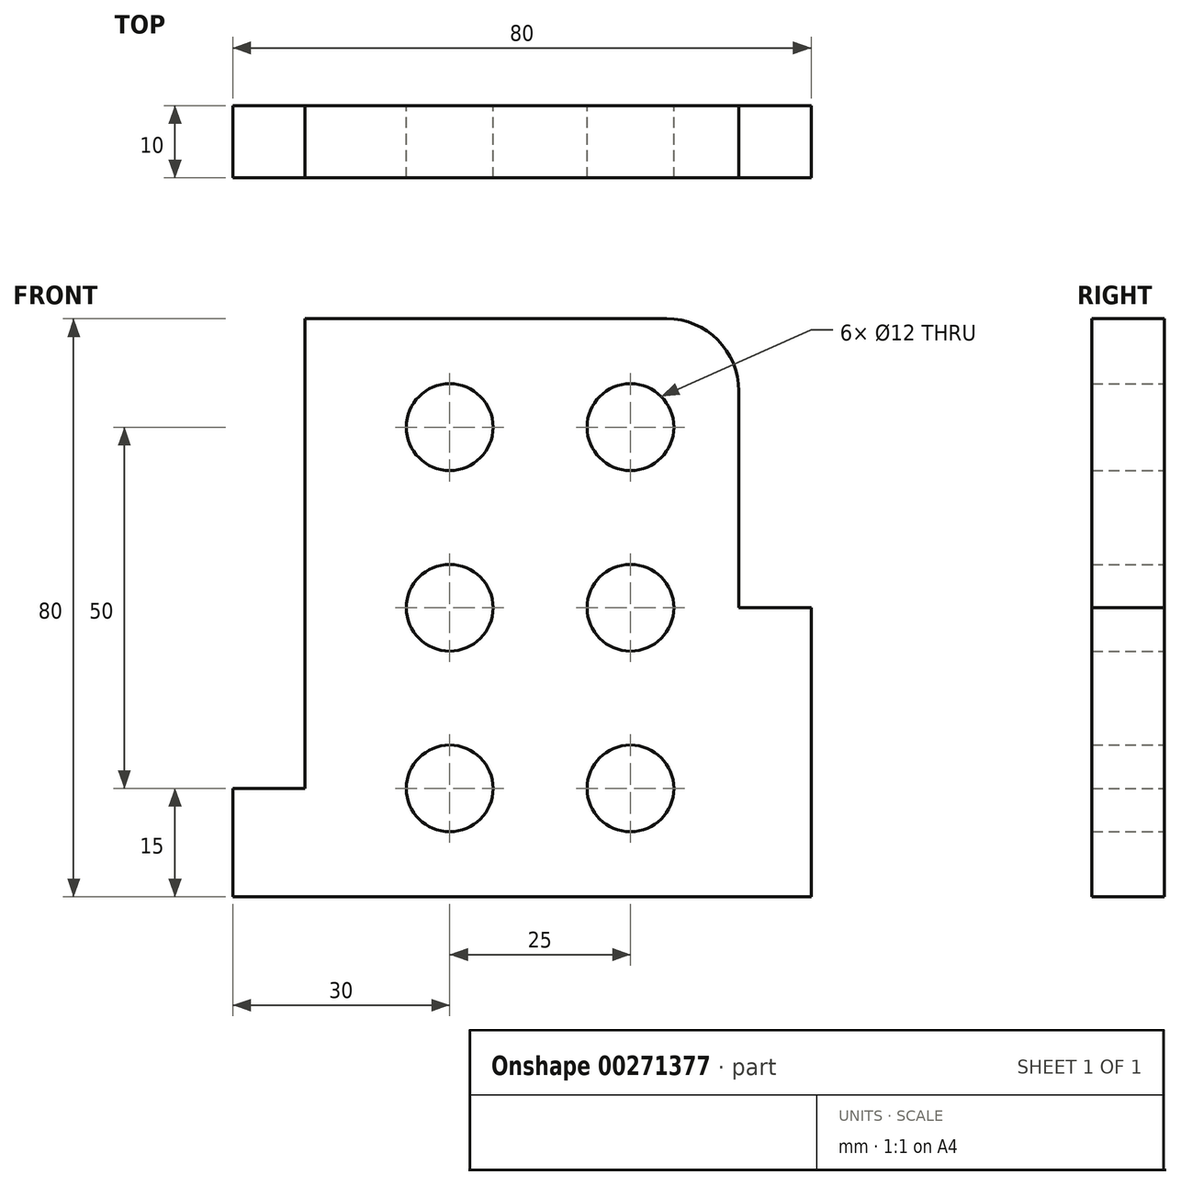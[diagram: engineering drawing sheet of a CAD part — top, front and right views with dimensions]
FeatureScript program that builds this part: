
annotation { "Feature Type Name" : "Feature", "Feature Type Description" : "" }
export const myFeature = defineFeature(function(context is Context, id is Id, definition is map)
    precondition{}
    {
        {
            var Q0;
            Q0=qCreatedBy(makeId("Front.planeOp"),FACE);
            var sketch = newSketch(context, id + "F0", { "sketchPlane" : qUnion([Q0])});
            skLineSegment(sketch, "E0", {"start": v(0, 0) * mm, "end": v(80, 0) * mm});
            skLineSegment(sketch, "E1", {"start": v(0, 0) * mm, "end": v(0, 15) * mm});
            skLineSegment(sketch, "E2", {"start": v(0, 15) * mm, "end": v(10, 15) * mm});
            skLineSegment(sketch, "E3", {"start": v(10, 15) * mm, "end": v(10, 80) * mm});
            skLineSegment(sketch, "E4", {"start": v(80, 0) * mm, "end": v(80, 40) * mm});
            skLineSegment(sketch, "E5", {"start": v(80, 40) * mm, "end": v(70, 40) * mm});
            skLineSegment(sketch, "E6", {"start": v(70, 40) * mm, "end": v(70, 70) * mm});
            skArc(sketch, "E7", {"start": v(70, 70) * mm, "mid": v(67.07, 77.07) * mm, "end": v(60, 80) * mm});
            skLineSegment(sketch, "E8", {"start": v(10, 80) * mm, "end": v(60, 80) * mm});
            skCircle(sketch, "E9", {"center": v(30, 15) * mm, "radius": 6 * mm});
            skCircle(sketch, "E10", {"center": v(55, 15) * mm, "radius": 6 * mm});
            skCircle(sketch, "E11", {"center": v(30, 40) * mm, "radius": 6 * mm});
            skCircle(sketch, "E12", {"center": v(55, 40) * mm, "radius": 6 * mm});
            skCircle(sketch, "E13", {"center": v(30, 65) * mm, "radius": 6 * mm});
            skCircle(sketch, "E14", {"center": v(55, 65) * mm, "radius": 6 * mm});
            skSolve(sketch);
        }
        {
            var Q0;
            Q0=makeQuery(id+"F0.imprint","IMPRINT",FACE,{"disambiguationData":[TD([[makeQuery(id+"F0.imprint","IMPRINT",EDGE,{"derivedFrom":sQuery(id+"F0.wireOp",EDGE,"E0")}),1.0]])]});
            extrude(context, id + "F1", {"entities" : qUnion([Q0]), "depth" : 10 * mm});
        }
    });
